# Revit family: CLighting - Luminii - Stenos - Suspended Track - Corner
name_source: partatom
category: Lighting Fixtures
units: mm (PartAtom-declared; Revit-internal decimal feet)

## family parameters
Cut with Voids When Loaded = No
Host = Face
Light Source = No
OmniClass Number = 23.80.70.11.14.21
OmniClass Title = Spots and Tracklight Specialties
Part Type = Normal
Room Calculation Point = No
Round Connector Dimension = Use Diameter
Shared = Yes

## types (1)
- Stenos Suspended - Corner Joint
    Apparent Load = 0 VA
    Assembly Code = D5020230
    Constraints = 1
    Default Elevation = 0' - 0"
    Depth = 0' - 1"
    Description = Suspended Trim Track System
    Environment = Indoor
    Finish = Metal - Luminii - Silver Anodized Aluminum
    Keynote = 26 50 00
    Length = 4' - 0"
    Load Classification = Other
    Manufacturer = Luminii
    Model = STH
    Product Page URL = https://www.luminii.com
    URL = https://www.luminii.com
    Version = 2020 - v1.0a
    Voltage = 0 V
    Warranty URL = https://www.luminii.com
    Width = 0' - 0 15/16"

## geometry (parser evidence)
native form markers: Sweep x7
no freeform markers — native parametric forms only
